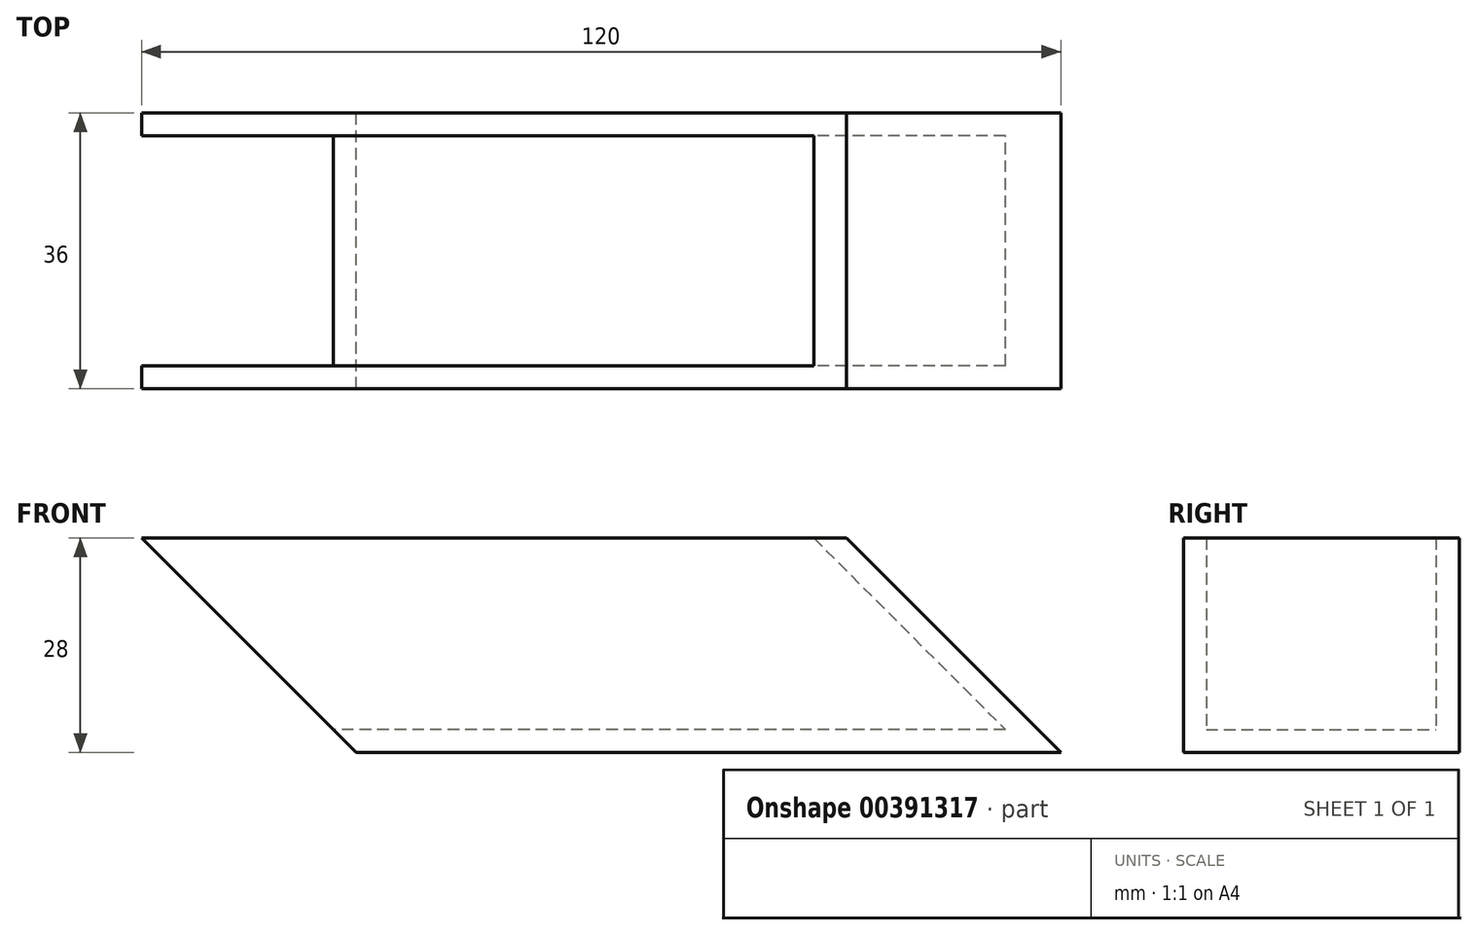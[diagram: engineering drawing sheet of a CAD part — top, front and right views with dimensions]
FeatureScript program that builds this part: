
annotation { "Feature Type Name" : "Feature", "Feature Type Description" : "" }
export const myFeature = defineFeature(function(context is Context, id is Id, definition is map)
    precondition{}
    {
        {
            var Q0;
            Q0=qCreatedBy(makeId("Front.planeOp"),FACE);
            var sketch = newSketch(context, id + "F0", { "sketchPlane" : qUnion([Q0])});
            skLineSegment(sketch, "E0", {"start": v(0, 0) * mm, "end": v(92, 0) * mm});
            skLineSegment(sketch, "E1", {"start": v(92, 0) * mm, "end": v(64, 28) * mm});
            skLineSegment(sketch, "E2", {"start": v(64, 28) * mm, "end": v(-28, 28) * mm});
            skLineSegment(sketch, "E3", {"start": v(-28, 28) * mm, "end": v(0, 0) * mm});
            skSolve(sketch);
        }
        {
            var Q0;
            Q0=makeQuery(id+"F0.imprint","IMPRINT",FACE,{"disambiguationData":[TD([[makeQuery(id+"F0.imprint","IMPRINT",EDGE,{"derivedFrom":sQuery(id+"F0.wireOp",EDGE,"E0")}),1.0]])]});
            extrude(context, id + "F1", {"entities" : qUnion([Q0]), "endBound" : BoundingType.SYMMETRIC, "depth" : 36 * mm, "offsetDistance" : 25 * mm});
        }
        {
            var Q0;
            Q0=qCreatedBy(makeId("Front.planeOp"),FACE);
            var sketch = newSketch(context, id + "F2", { "sketchPlane" : qUnion([Q0])});
            skLineSegment(sketch, "E4", {"start": v(58.34, 29.41) * mm, "end": v(84.76, 3) * mm});
            skLineSegment(sketch, "E5", {"start": v(-33.56, 29.49) * mm, "end": v(58.34, 29.41) * mm});
            skLineSegment(sketch, "E6", {"start": v(84.76, 3) * mm, "end": v(-6.53, 3) * mm});
            skLineSegment(sketch, "E7", {"start": v(-6.53, 3) * mm, "end": v(-33.56, 29.49) * mm});
            skSolve(sketch);
        }
        {
            var Q0;
            Q0 = qSketchRegion(id + "F2", true);
            extrude(context, id + "F3", {"entities" : qUnion([Q0]), "operationType" : NewBodyOperationType.REMOVE, "endBound" : BoundingType.SYMMETRIC, "depth" : 30 * mm, "offsetDistance" : 25 * mm});
        }
    });
